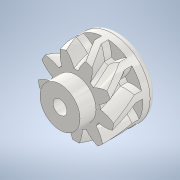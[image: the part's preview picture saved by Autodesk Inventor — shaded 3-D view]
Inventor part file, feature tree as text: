
AUTODESK INVENTOR PART (.ipt)
format: ipt  version: 2022 (Build 260153070, 153G)  size: 465,408 bytes
history: native  units: mm (DEFAULTED — no unit token found)
features: sketch x6, extrude x5, plane x3, other x3, fillet x1, projected_geometry x1
ambient origin geometry x8: Origin, YZ Plane, XZ Plane, XY Plane, X Axis, Y Axis, Z Axis, Center Point
bodies: Solid1 (feature_tree)
feature tree (19):
  extrude  "Extrusion1"  Depth=3.0mm TaperAngle=0.0deg
  plane  "Work Plane2"
  plane  "Work Plane8"
  plane  "Work Plane9"
  other  "Spur Gear"
  extrude  "Extrusion2"  Depth=10.0mm TaperAngle=0.0deg
  extrude  "Extrusion3"  Depth=3.490659mm TaperAngle=0.0deg
  fillet  "Fillet1"  [1 undecoded]
  extrude  "Extrusion5"  Depth=20.0mm
  extrude  "Extrusion4"  TaperAngle=0.0deg  [1 undecoded]
  sketch  "Sketch1"  dims[d0=10.350115mm d1=3.0mm d2=0.0mm]
  sketch  "Sketch2"  dims[d3=7.944321mm d4=10.0mm d5=0.0mm]
  other  "Srf1"
  sketch  "Sketch3"  dims[d16=20.0mm d17=0.0mm d34=3.490659mm d39=0.0mm]
  projected_geometry  "Projected Loop1"
  sketch  "Sketch4"  dims[d41=0.0mm d43=20.0mm]
  sketch  "Sketch5"  dims[d46=20.0mm d47=0.0mm d48=0.0mm]
  sketch  "Sketch6"  dims[d52=1.5mm d53=1.0mm d54=0.0mm d55=6.15mm d56=2.0mm d57=0.0mm d58=1.0mm d59=1.9mm d60=2.9mm d61=0.0mm d62=2.2mm d63=0.0mm d64=2.0mm d65=0.0mm d66=3.75mm]
  other  "Pitch Diameter"
note: 2 required parameter values undecoded (feature->parameter linkage not recoverable at this tier; creation-order binding heuristic only, values carry confidence <= 0.55)
